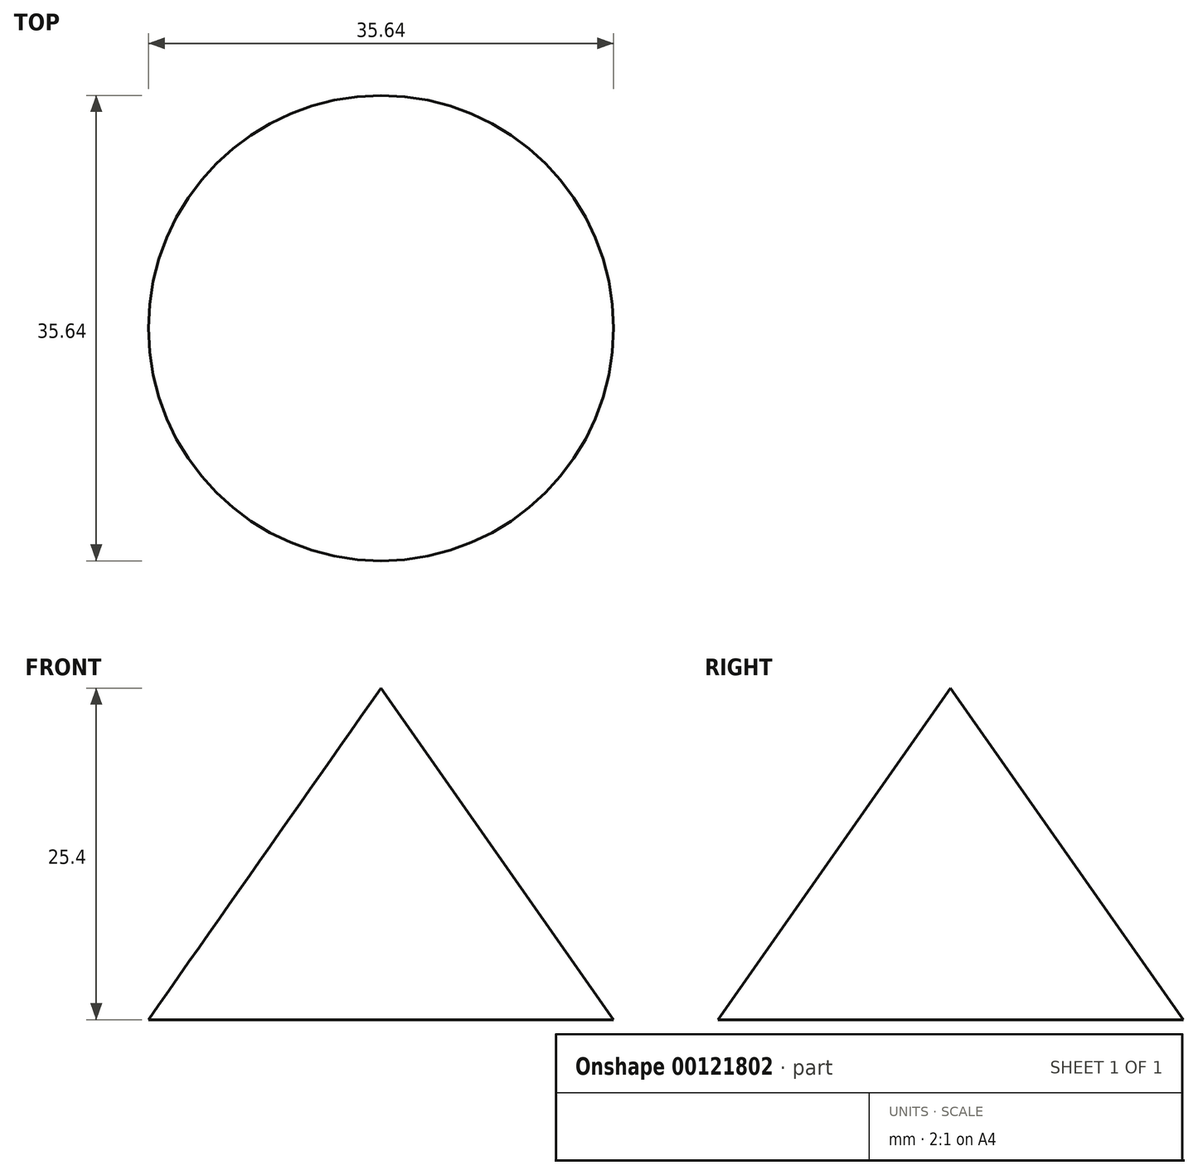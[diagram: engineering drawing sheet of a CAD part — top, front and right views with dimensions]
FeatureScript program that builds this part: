
annotation { "Feature Type Name" : "Feature", "Feature Type Description" : "" }
export const myFeature = defineFeature(function(context is Context, id is Id, definition is map)
    precondition{}
    {
        {
            var Q0;
            Q0=qCreatedBy(makeId("Top.planeOp"),FACE);
            var sketch = newSketch(context, id + "F0", { "sketchPlane" : qUnion([Q0])});
            skCircle(sketch, "E0", {"center": v(0, 0) * mm, "radius": 17.82 * mm});
            skSolve(sketch);
        }
        {
            var Q0;
            Q0=makeQuery(id+"F0.imprint","IMPRINT",FACE,{"disambiguationData":[TD([[makeQuery(id+"F0.imprint","IMPRINT",EDGE,{"derivedFrom":sQuery(id+"F0.wireOp",EDGE,"E0")}),1.0]])]});
            cPlane(context, id + "F1", {"entities" : qUnion([Q0]), "cplaneType" : CPlaneType.OFFSET, "offset" : 25.4 * mm, "width" : 152.4 * mm, "height" : 152.4 * mm});
        }
        {
            var Q0;
            Q0=qCreatedBy(id+"F1.planeOp",FACE);
            var sketch = newSketch(context, id + "F2", { "sketchPlane" : qUnion([Q0])});
            skCircle(sketch, "E1", {"center": v(0, 0) * mm, "radius": 1.87 * mm});
            skSolve(sketch);
        }
        {
            var Q0;
            Q0=makeQuery(id+"F0.imprint","IMPRINT",FACE,{"disambiguationData":[TD([[makeQuery(id+"F0.imprint","IMPRINT",EDGE,{"derivedFrom":sQuery(id+"F0.wireOp",EDGE,"E0")}),1.0]])]});
            var Q1;
            Q1=sQuery(id+"F2.wireOp",VERTEX,"E1.center");
            loft(context, id + "F3", {"sheetProfilesArray" : [{ "sheetProfileEntities" : qUnion([Q0]) }, { "sheetProfileEntities" : qUnion([Q1]) }]});
        }
    });
